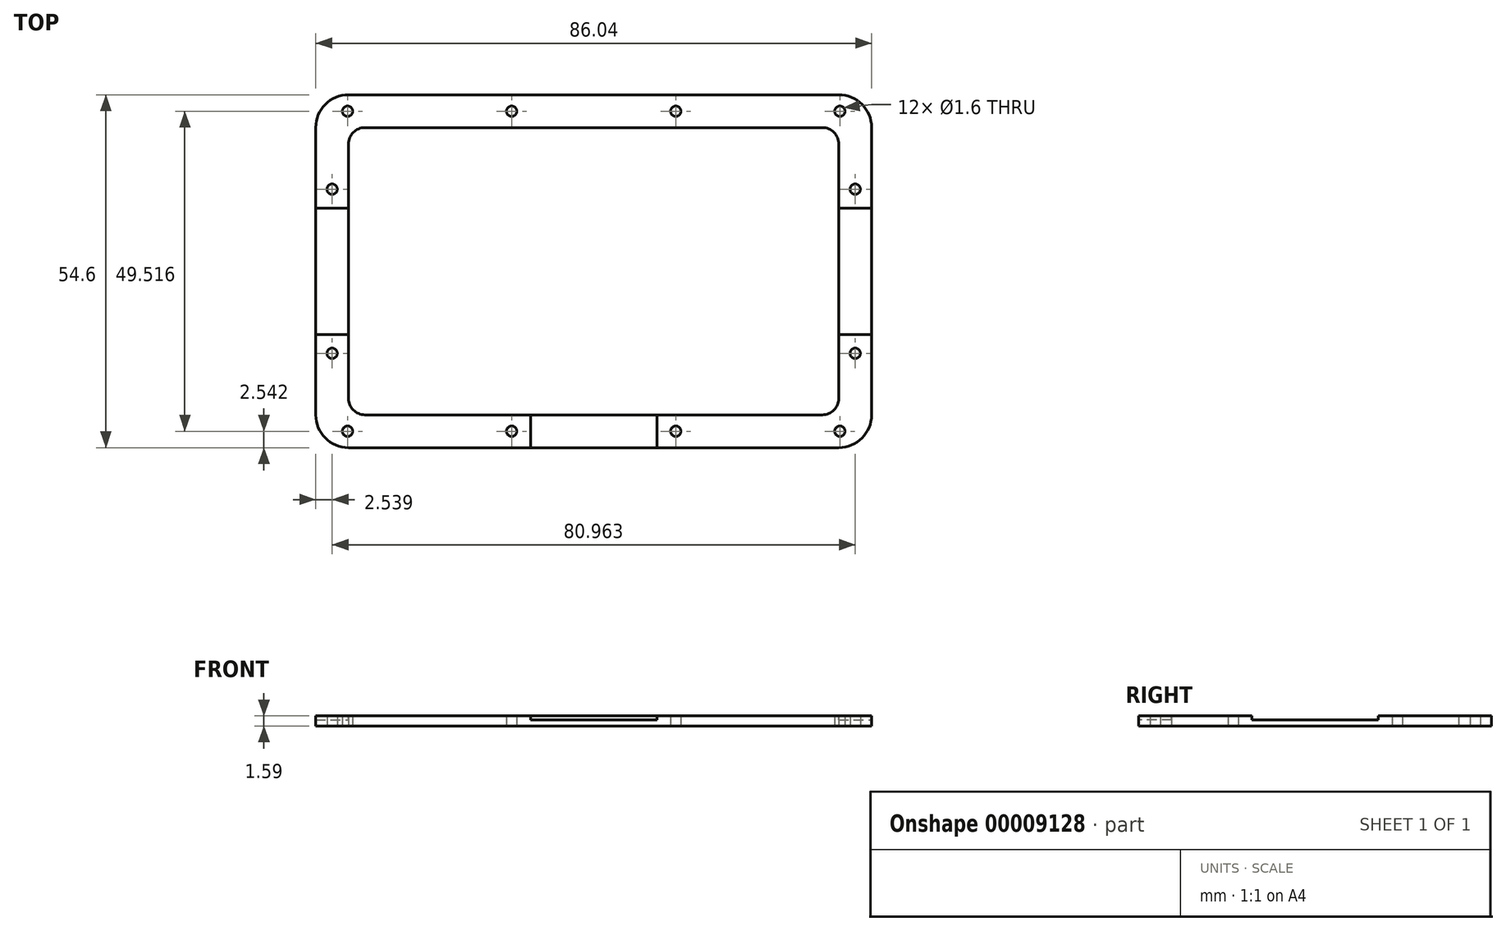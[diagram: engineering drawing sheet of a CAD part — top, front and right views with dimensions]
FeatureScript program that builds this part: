
annotation { "Feature Type Name" : "Feature", "Feature Type Description" : "" }
export const myFeature = defineFeature(function(context is Context, id is Id, definition is map)
    precondition{}
    {
        {
            var Q0;
            Q0=qCreatedBy(makeId("Top.planeOp"),FACE);
            var sketch = newSketch(context, id + "F0", { "sketchPlane" : qUnion([Q0])});
            skLineSegment(sketch, "E0.bottom", {"start": v(-43.02, 27.3) * mm, "end": v(43.02, 27.3) * mm});
            skLineSegment(sketch, "E0.top", {"start": v(-43.02, -27.3) * mm, "end": v(43.02, -27.3) * mm});
            skLineSegment(sketch, "E0.left", {"start": v(-43.02, 27.3) * mm, "end": v(-43.02, -27.3) * mm});
            skLineSegment(sketch, "E0.right", {"start": v(43.02, 27.3) * mm, "end": v(43.02, -27.3) * mm});
            skLineSegment(sketch, "E1", {"start": v(0, 28.85) * mm, "end": v(0, -30.48) * mm, "construction": true});
            skLineSegment(sketch, "E2", {"start": v(-35.92, 0) * mm, "end": v(38.92, 0) * mm, "construction": true});
            skLineSegment(sketch, "E3.bottom", {"start": v(-37.94, 22.23) * mm, "end": v(37.94, 22.23) * mm});
            skLineSegment(sketch, "E3.top", {"start": v(-37.94, -22.23) * mm, "end": v(37.94, -22.23) * mm});
            skLineSegment(sketch, "E3.left", {"start": v(-37.94, 22.23) * mm, "end": v(-37.94, -22.23) * mm});
            skLineSegment(sketch, "E3.right", {"start": v(37.94, 22.22) * mm, "end": v(37.94, -22.22) * mm});
            skCircle(sketch, "E4", {"center": v(-38.1, 24.76) * mm, "radius": 0.8 * mm});
            skCircle(sketch, "E5.0.MirrorC", {"center": v(-38.1, -24.76) * mm, "radius": 0.8 * mm});
            skCircle(sketch, "E6.1.0.0", {"center": v(-12.7, 24.76) * mm, "radius": 0.8 * mm});
            skCircle(sketch, "E6.2.0.0", {"center": v(12.7, 24.76) * mm, "radius": 0.8 * mm});
            skCircle(sketch, "E6.3.0.0", {"center": v(38.1, 24.76) * mm, "radius": 0.8 * mm});
            skLineSegment(sketch, "E6.direction1", {"start": v(-38.1, 24.76) * mm, "end": v(-12.7, 24.76) * mm, "construction": true});
            skCircle(sketch, "E7.1.0.0", {"center": v(-12.7, -24.76) * mm, "radius": 0.8 * mm});
            skCircle(sketch, "E7.2.0.0", {"center": v(12.7, -24.76) * mm, "radius": 0.8 * mm});
            skCircle(sketch, "E7.3.0.0", {"center": v(38.1, -24.76) * mm, "radius": 0.8 * mm});
            skLineSegment(sketch, "E7.direction1", {"start": v(-38.1, -24.76) * mm, "end": v(-12.7, -24.76) * mm, "construction": true});
            skCircle(sketch, "E8", {"center": v(-40.48, 12.7) * mm, "radius": 0.8 * mm});
            skCircle(sketch, "E9.0.1.0", {"center": v(-40.48, -12.7) * mm, "radius": 0.8 * mm});
            skLineSegment(sketch, "E9.direction1", {"start": v(-40.48, 12.7) * mm, "end": v(-21.14, 12.74) * mm, "construction": true});
            skLineSegment(sketch, "E9.direction2", {"start": v(-40.48, 12.7) * mm, "end": v(-40.48, -12.7) * mm, "construction": true});
            skCircle(sketch, "E10.0.MirrorC", {"center": v(40.48, -12.7) * mm, "radius": 0.8 * mm});
            skCircle(sketch, "E10.1.MirrorC", {"center": v(40.48, 12.7) * mm, "radius": 0.8 * mm});
            skSolve(sketch);
        }
        {
            var Q0;
            Q0=makeQuery(id+"F0.imprint","IMPRINT",FACE,{"disambiguationData":[TD([[makeQuery(id+"F0.imprint","IMPRINT",EDGE,{"derivedFrom":sQuery(id+"F0.wireOp",EDGE,"E0.bottom")}),-1.0]])]});
            extrude(context, id + "F1", {"entities" : qUnion([Q0]), "depth" : 1.59 * mm});
        }
        {
            var Q0;
            Q0=makeQuery(id+"F1.opExtrude","SWEPT_EDGE",EDGE,{"disambiguationData":[OSD([sQuery(id+"F0.wireOp",EDGE,"E0.bottom"),sQuery(id+"F0.wireOp",EDGE,"E0.left")])]});
            var Q1;
            Q1=makeQuery(id+"F1.opExtrude","SWEPT_EDGE",EDGE,{"disambiguationData":[OSD([sQuery(id+"F0.wireOp",EDGE,"E0.top"),sQuery(id+"F0.wireOp",EDGE,"E0.left")])]});
            var Q2;
            Q2=makeQuery(id+"F1.opExtrude","SWEPT_EDGE",EDGE,{"disambiguationData":[OSD([sQuery(id+"F0.wireOp",EDGE,"E0.top"),sQuery(id+"F0.wireOp",EDGE,"E0.right")])]});
            var Q3;
            Q3=makeQuery(id+"F1.opExtrude","SWEPT_EDGE",EDGE,{"disambiguationData":[OSD([sQuery(id+"F0.wireOp",EDGE,"E0.bottom"),sQuery(id+"F0.wireOp",EDGE,"E0.right")])]});
            fillet(context, id + "F2", {"entities" : qUnion([Q0, Q1, Q2, Q3]), "radius" : 5.08 * mm, "tangentPropagation" : true, "allowEdgeOverflow" : false});
        }
        {
            var Q0;
            Q0=makeQuery(id+"F1.opExtrude","SWEPT_EDGE",EDGE,{"disambiguationData":[OSD([sQuery(id+"F0.wireOp",EDGE,"E3.bottom"),sQuery(id+"F0.wireOp",EDGE,"E3.left")])]});
            var Q1;
            Q1=makeQuery(id+"F1.opExtrude","SWEPT_EDGE",EDGE,{"disambiguationData":[OSD([sQuery(id+"F0.wireOp",EDGE,"E3.bottom"),sQuery(id+"F0.wireOp",EDGE,"E3.right")])]});
            var Q2;
            Q2=makeQuery(id+"F1.opExtrude","SWEPT_EDGE",EDGE,{"disambiguationData":[OSD([sQuery(id+"F0.wireOp",EDGE,"E3.top"),sQuery(id+"F0.wireOp",EDGE,"E3.left")])]});
            var Q3;
            Q3=makeQuery(id+"F1.opExtrude","SWEPT_EDGE",EDGE,{"disambiguationData":[OSD([sQuery(id+"F0.wireOp",EDGE,"E3.top"),sQuery(id+"F0.wireOp",EDGE,"E3.right")])]});
            fillet(context, id + "F3", {"entities" : qUnion([Q0, Q1, Q2, Q3]), "radius" : 2.54 * mm, "tangentPropagation" : true, "allowEdgeOverflow" : false});
        }
        {
            var Q0;
            Q0=makeQuery(id+"F1.opExtrude","CAP_FACE",FACE,{"disambiguationData":[OSD([sQuery(id+"F0.wireOp",EDGE,"E0.bottom"),sQuery(id+"F0.wireOp",EDGE,"E0.top"),sQuery(id+"F0.wireOp",EDGE,"E0.left"),sQuery(id+"F0.wireOp",EDGE,"E0.right"),sQuery(id+"F0.wireOp",EDGE,"E3.bottom"),sQuery(id+"F0.wireOp",EDGE,"E3.top"),sQuery(id+"F0.wireOp",EDGE,"E3.left"),sQuery(id+"F0.wireOp",EDGE,"E3.right"),sQuery(id+"F0.wireOp",EDGE,"E4"),sQuery(id+"F0.wireOp",EDGE,"E5.0.MirrorC"),sQuery(id+"F0.wireOp",EDGE,"E6.1.0.0"),sQuery(id+"F0.wireOp",EDGE,"E6.2.0.0"),sQuery(id+"F0.wireOp",EDGE,"E6.3.0.0"),sQuery(id+"F0.wireOp",EDGE,"E7.1.0.0"),sQuery(id+"F0.wireOp",EDGE,"E7.2.0.0"),sQuery(id+"F0.wireOp",EDGE,"E7.3.0.0"),sQuery(id+"F0.wireOp",EDGE,"E8"),sQuery(id+"F0.wireOp",EDGE,"E9.0.1.0"),sQuery(id+"F0.wireOp",EDGE,"E10.1.MirrorC"),sQuery(id+"F0.wireOp",EDGE,"E10.0.MirrorC")])],"isStart":false});
            var sketch = newSketch(context, id + "F4", { "sketchPlane" : qUnion([Q0])});
            skLineSegment(sketch, "E11", {"start": v(-43.02, 9.78) * mm, "end": v(-37.94, 9.78) * mm});
            skLineSegment(sketch, "E12", {"start": v(-43.02, -9.78) * mm, "end": v(-37.94, -9.78) * mm});
            skLineSegment(sketch, "E13", {"start": v(-9.78, -22.23) * mm, "end": v(-9.78, -27.3) * mm});
            skLineSegment(sketch, "E14", {"start": v(9.78, -22.23) * mm, "end": v(9.78, -27.3) * mm});
            skLineSegment(sketch, "E15.0", {"start": v(-43.02, 9.78) * mm, "end": v(-43.02, -9.78) * mm});
            skLineSegment(sketch, "E16.0", {"start": v(-37.94, 9.78) * mm, "end": v(-37.94, -9.78) * mm});
            skLineSegment(sketch, "E17.0", {"start": v(-9.78, -22.23) * mm, "end": v(9.78, -22.23) * mm});
            skLineSegment(sketch, "E18.0", {"start": v(-9.78, -27.3) * mm, "end": v(9.78, -27.3) * mm});
            skLineSegment(sketch, "E19.0", {"start": v(37.94, 9.78) * mm, "end": v(37.94, -9.78) * mm});
            skLineSegment(sketch, "E20.0", {"start": v(43.02, 9.78) * mm, "end": v(43.02, -9.78) * mm});
            skLineSegment(sketch, "E21.trimOffspring", {"start": v(37.94, 9.78) * mm, "end": v(43.02, 9.78) * mm});
            skLineSegment(sketch, "E22.trimOffspring", {"start": v(37.94, -9.78) * mm, "end": v(43.02, -9.78) * mm});
            skSolve(sketch);
        }
        {
            var Q0;
            Q0 = qSketchRegion(id + "F4", true);
            extrude(context, id + "F5", {"entities" : qUnion([Q0]), "operationType" : NewBodyOperationType.REMOVE, "oppositeDirection" : true, "depth" : 0.64 * mm});
        }
    });
